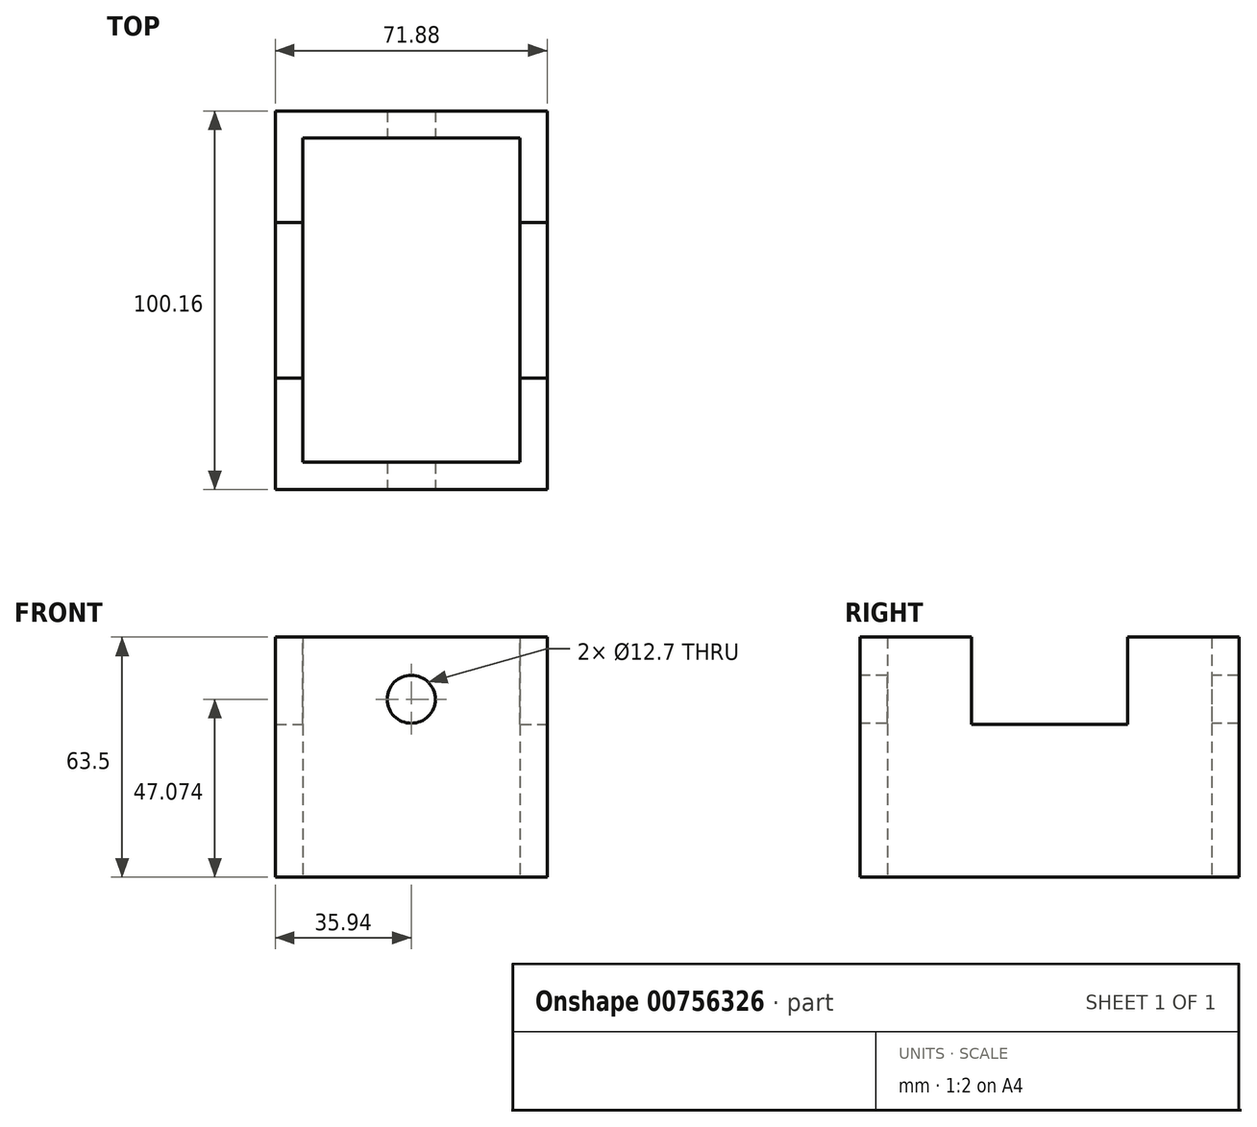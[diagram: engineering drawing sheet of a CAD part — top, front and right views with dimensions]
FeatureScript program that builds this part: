
annotation { "Feature Type Name" : "Feature", "Feature Type Description" : "" }
export const myFeature = defineFeature(function(context is Context, id is Id, definition is map)
    precondition{}
    {
        {
            var Q0;
            Q0=qCreatedBy(makeId("Top.planeOp"),FACE);
            var sketch = newSketch(context, id + "F0", { "sketchPlane" : qUnion([Q0])});
            skLineSegment(sketch, "E0", {"start": v(-35.94, 0) * mm, "end": v(-35.94, 50.08) * mm});
            skLineSegment(sketch, "E1", {"start": v(-35.94, 50.08) * mm, "end": v(0, 50.08) * mm});
            skLineSegment(sketch, "E2.MirrorCS", {"start": v(35.94, 0) * mm, "end": v(35.94, 50.08) * mm});
            skLineSegment(sketch, "E3.MirrorCS", {"start": v(35.94, 50.08) * mm, "end": v(0, 50.08) * mm});
            skLineSegment(sketch, "E4.MirrorCS", {"start": v(-35.94, -50.08) * mm, "end": v(0, -50.08) * mm});
            skLineSegment(sketch, "E5.MirrorCS", {"start": v(35.94, 0) * mm, "end": v(35.94, -50.08) * mm});
            skLineSegment(sketch, "E6.MirrorCS", {"start": v(35.94, -50.08) * mm, "end": v(0, -50.08) * mm});
            skLineSegment(sketch, "E7.MirrorCS", {"start": v(-35.94, 0) * mm, "end": v(-35.94, -50.08) * mm});
            skLineSegment(sketch, "E8", {"start": v(-28.73, 0) * mm, "end": v(-28.73, 42.86) * mm});
            skLineSegment(sketch, "E9", {"start": v(-28.73, 42.86) * mm, "end": v(0, 42.86) * mm});
            skLineSegment(sketch, "E10.MirrorCS", {"start": v(28.73, 0) * mm, "end": v(28.73, 42.86) * mm});
            skLineSegment(sketch, "E11.MirrorCS", {"start": v(28.73, 42.86) * mm, "end": v(0, 42.86) * mm});
            skLineSegment(sketch, "E12.MirrorCS", {"start": v(28.73, 0) * mm, "end": v(28.73, -42.86) * mm});
            skLineSegment(sketch, "E13.MirrorCS", {"start": v(28.73, -42.86) * mm, "end": v(0, -42.86) * mm});
            skLineSegment(sketch, "E14.MirrorCS", {"start": v(-28.73, 0) * mm, "end": v(-28.73, -42.86) * mm});
            skLineSegment(sketch, "E15.MirrorCS", {"start": v(-28.73, -42.86) * mm, "end": v(0, -42.86) * mm});
            skSolve(sketch);
        }
        {
            var Q0;
            Q0=makeQuery(id+"F0.imprint","IMPRINT",FACE,{"disambiguationData":[TD([[makeQuery(id+"F0.imprint","IMPRINT",EDGE,{"derivedFrom":sQuery(id+"F0.wireOp",EDGE,"E1")}),-1.0]])]});
            extrude(context, id + "F1", {"entities" : qUnion([Q0]), "depth" : 63.5 * mm, "offsetDistance" : 25.4 * mm});
        }
        {
            var Q0;
            Q0=makeQuery(id+"F1.opExtrude","SWEPT_FACE",FACE,{"disambiguationData":[OSD([sQuery(id+"F0.wireOp",EDGE,"E2.MirrorCS"),sQuery(id+"F0.wireOp",EDGE,"E5.MirrorCS")])]});
            var sketch = newSketch(context, id + "F2", { "sketchPlane" : qUnion([Q0])});
            skLineSegment(sketch, "E16", {"start": v(-20.6, 63.5) * mm, "end": v(-20.6, 40.46) * mm});
            skLineSegment(sketch, "E17", {"start": v(-20.6, 40.46) * mm, "end": v(0, 40.46) * mm});
            skLineSegment(sketch, "E18.MirrorCS", {"start": v(20.6, 40.46) * mm, "end": v(0, 40.46) * mm});
            skLineSegment(sketch, "E19.MirrorCS", {"start": v(20.6, 63.5) * mm, "end": v(20.6, 40.46) * mm});
            skSolve(sketch);
        }
        {
            var Q0;
            {var subQ1=sQuery(id+"F2.wireOp",EDGE,"E16");Q0=makeQuery(id+"F2.imprint","IMPRINT",FACE,{"disambiguationData":[TD([[makeQuery(id+"F2.imprint","IMPRINT",EDGE,{"derivedFrom":subQ1}),1.0]])]});}
            extrude(context, id + "F3", {"entities" : qUnion([Q0]), "operationType" : NewBodyOperationType.REMOVE, "oppositeDirection" : true, "depth" : 127 * mm, "offsetDistance" : 25.4 * mm});
        }
        {
            var Q0;
            Q0=makeQuery(id+"F1.opExtrude","SWEPT_FACE",FACE,{"disambiguationData":[OSD([sQuery(id+"F0.wireOp",EDGE,"E4.MirrorCS"),sQuery(id+"F0.wireOp",EDGE,"E6.MirrorCS")])]});
            var sketch = newSketch(context, id + "F4", { "sketchPlane" : qUnion([Q0])});
            skPoint(sketch, "E20", {"position": v(0, 47.07) * mm});
            skPoint(sketch, "E20.positionSnap0", {"position": v(0, 63.5) * mm});
            skSolve(sketch);
        }
        {
            var Q0;
            Q0=sQuery(id+"F4.wireOp",VERTEX,"E20");
            var Q1;
            Q1=makeQuery(id+"F1.opExtrude","SWEPT_BODY",BODY,{"disambiguationData":[OSD([sQuery(id+"F0.wireOp",EDGE,"E1"),sQuery(id+"F0.wireOp",EDGE,"E3.MirrorCS"),sQuery(id+"F0.wireOp",EDGE,"E2.MirrorCS"),sQuery(id+"F0.wireOp",EDGE,"E0"),sQuery(id+"F0.wireOp",EDGE,"E5.MirrorCS"),sQuery(id+"F0.wireOp",EDGE,"E7.MirrorCS"),sQuery(id+"F0.wireOp",EDGE,"E4.MirrorCS"),sQuery(id+"F0.wireOp",EDGE,"E6.MirrorCS"),sQuery(id+"F0.wireOp",EDGE,"E8"),sQuery(id+"F0.wireOp",EDGE,"E9"),sQuery(id+"F0.wireOp",EDGE,"E10.MirrorCS"),sQuery(id+"F0.wireOp",EDGE,"E11.MirrorCS"),sQuery(id+"F0.wireOp",EDGE,"E12.MirrorCS"),sQuery(id+"F0.wireOp",EDGE,"E13.MirrorCS"),sQuery(id+"F0.wireOp",EDGE,"E14.MirrorCS"),sQuery(id+"F0.wireOp",EDGE,"E15.MirrorCS")])]});
            hole(context, id + "F5", {"style" : HoleStyle.SIMPLE, "endStyle" : HoleEndStyle.THROUGH, "holeDiameter" : 12.7 * mm, "majorDiameter" : 6.35 * mm, "isTappedThrough" : true, "tappedDepth" : 12.7 * mm, "tapClearance" : 3, "locations" : qUnion([Q0]), "scope" : qUnion([Q1])});
        }
    });
